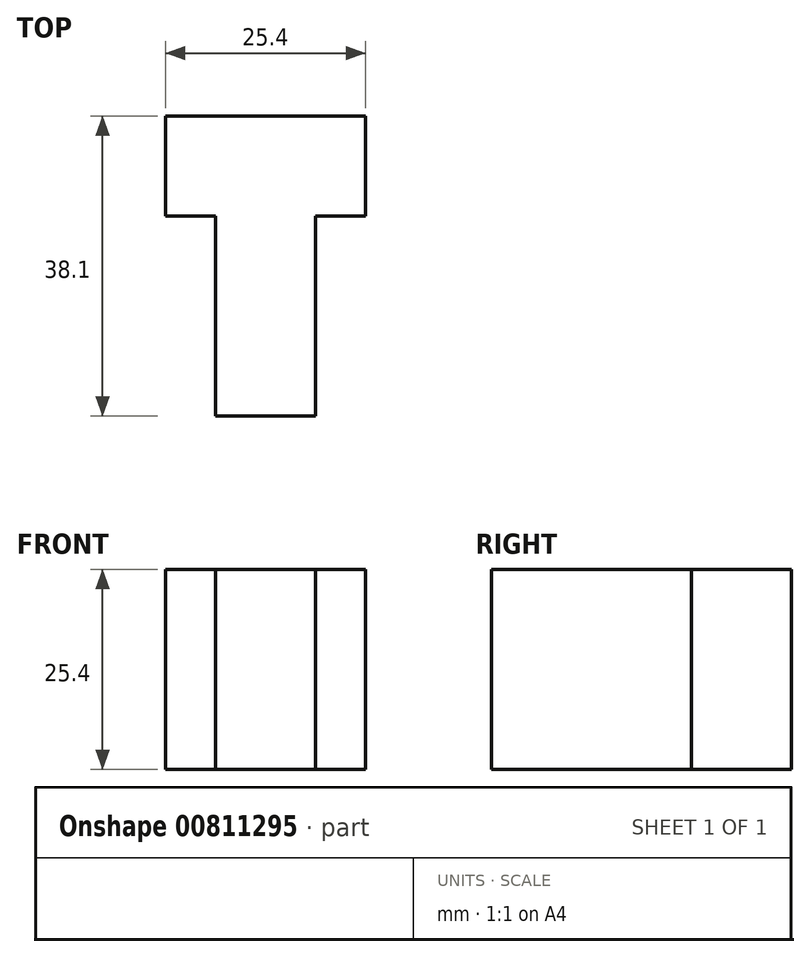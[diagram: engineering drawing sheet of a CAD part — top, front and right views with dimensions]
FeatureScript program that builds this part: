
annotation { "Feature Type Name" : "Feature", "Feature Type Description" : "" }
export const myFeature = defineFeature(function(context is Context, id is Id, definition is map)
    precondition{}
    {
        {
            var Q0;
            Q0=qCreatedBy(makeId("Top.planeOp"),FACE);
            var sketch = newSketch(context, id + "F0", { "sketchPlane" : qUnion([Q0])});
            skLineSegment(sketch, "E0", {"start": v(0, 0) * mm, "end": v(6.35, 0) * mm});
            skLineSegment(sketch, "E1", {"start": v(6.35, 0) * mm, "end": v(6.35, 12.7) * mm});
            skLineSegment(sketch, "E2", {"start": v(6.35, 12.7) * mm, "end": v(-19.05, 12.7) * mm});
            skLineSegment(sketch, "E3", {"start": v(-19.05, 12.7) * mm, "end": v(-19.05, 0) * mm});
            skLineSegment(sketch, "E4", {"start": v(-19.05, 0) * mm, "end": v(-12.7, 0) * mm});
            skLineSegment(sketch, "E5", {"start": v(-12.7, 0) * mm, "end": v(-12.7, -25.4) * mm});
            skLineSegment(sketch, "E6", {"start": v(-12.7, -25.4) * mm, "end": v(0, -25.4) * mm});
            skLineSegment(sketch, "E7", {"start": v(0, -25.4) * mm, "end": v(0, 0) * mm});
            skSolve(sketch);
        }
        {
            var Q0;
            Q0 = qSketchRegion(id + "F0", true);
            extrude(context, id + "F1", {"entities" : qUnion([Q0]), "depth" : 25.4 * mm, "offsetDistance" : 25.4 * mm});
        }
    });
